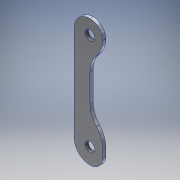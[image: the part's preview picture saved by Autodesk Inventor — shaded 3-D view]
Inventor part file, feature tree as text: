
AUTODESK INVENTOR PART (.ipt)
format: ipt  version: 2016 (Build 200138000, 138)  size: 147,968 bytes
history: native  units: in
note: dims shown in document units (in); Inventor stores cm internally (conversion verified against a paired STEP export)
features: fillet x3, extrude x1, sketch x1
ambient origin geometry x8: Origin, YZ Plane, XZ Plane, XY Plane, X Axis, Y Axis, Z Axis, Center Point
bodies: Body1 (feature_tree)
feature tree (5):
  extrude  "Extrusion2"  Depth=0.1575in
  fillet  "Fillet4"  Radius=0.1969in
  fillet  "Fillet6"  Radius=1.5748in
  fillet  "Fillet7"  Radius=0.1772in
  sketch  "Sketch3"  dims[d22=0.0394in d23=0.0in d24=0.1575in d26=0.1969in d27=1.5748in d28=0.1772in d29=0.0984in d32=0.0197in d33=0.3071in]
